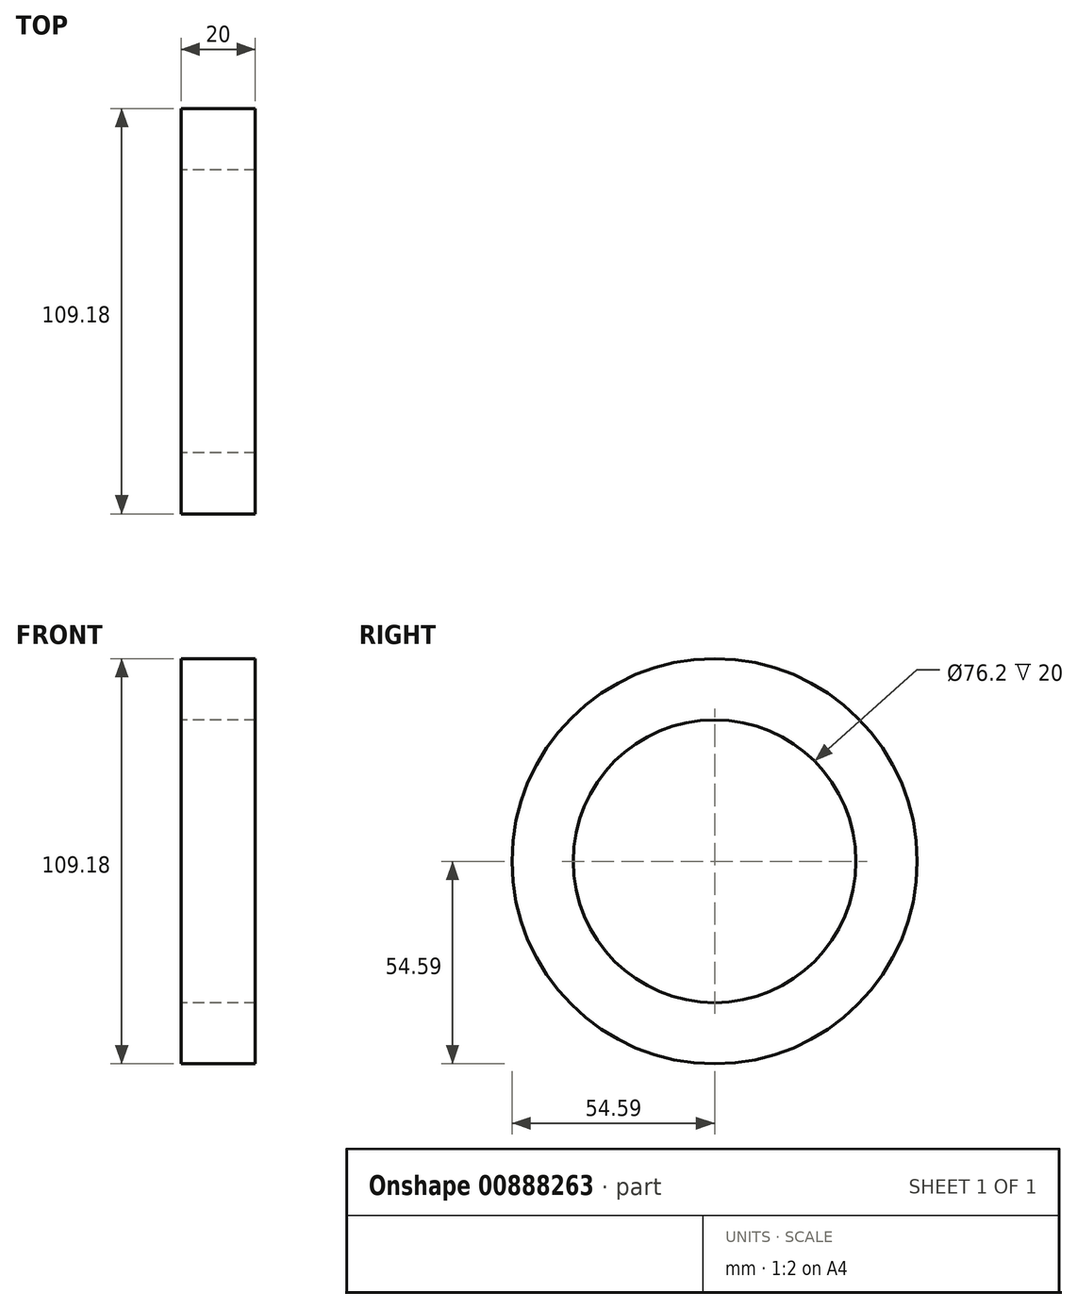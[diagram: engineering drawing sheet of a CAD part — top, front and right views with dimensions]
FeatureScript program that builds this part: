
annotation { "Feature Type Name" : "Feature", "Feature Type Description" : "" }
export const myFeature = defineFeature(function(context is Context, id is Id, definition is map)
    precondition{}
    {
        {
            var Q0;
            Q0=qCreatedBy(makeId("Right.planeOp"),FACE);
            var sketch = newSketch(context, id + "F0", { "sketchPlane" : qUnion([Q0])});
            skCircle(sketch, "E0", {"center": v(0, 0) * mm, "radius": 38.1 * mm});
            skCircle(sketch, "E1", {"center": v(0, 0) * mm, "radius": 54.59 * mm});
            skSolve(sketch);
        }
        {
            var Q0;
            Q0=makeQuery(id+"F0.imprint","IMPRINT",FACE,{"disambiguationData":[TD([[makeQuery(id+"F0.imprint","IMPRINT",EDGE,{"derivedFrom":sQuery(id+"F0.wireOp",EDGE,"E0")}),-1.0]])]});
            extrude(context, id + "F1", {"entities" : qUnion([Q0]), "depth" : 20 * mm, "offsetDistance" : 25 * mm});
        }
    });
